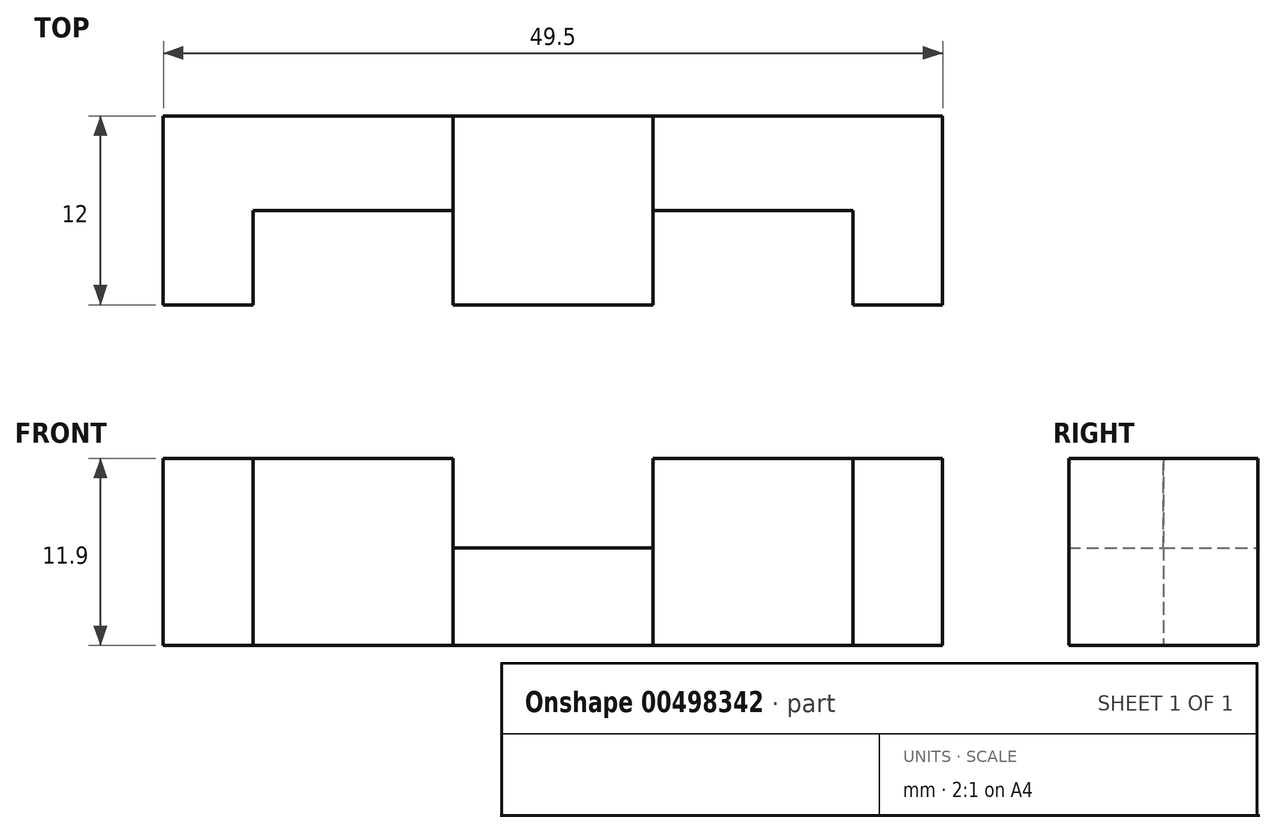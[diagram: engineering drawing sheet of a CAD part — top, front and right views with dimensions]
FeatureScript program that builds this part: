
annotation { "Feature Type Name" : "Feature", "Feature Type Description" : "" }
export const myFeature = defineFeature(function(context is Context, id is Id, definition is map)
    precondition{}
    {
        {
            var Q0;
            Q0=qCreatedBy(makeId("Front.planeOp"),FACE);
            var sketch = newSketch(context, id + "F0", { "sketchPlane" : qUnion([Q0])});
            skLineSegment(sketch, "E0.bottom", {"start": v(-12.84, 9.96) * mm, "end": v(36.66, 9.96) * mm});
            skLineSegment(sketch, "E0.top", {"start": v(-12.84, -1.94) * mm, "end": v(36.66, -1.94) * mm});
            skLineSegment(sketch, "E0.left", {"start": v(-12.84, 9.96) * mm, "end": v(-12.84, -1.94) * mm});
            skLineSegment(sketch, "E0.right", {"start": v(36.66, 9.96) * mm, "end": v(36.66, -1.94) * mm});
            skLineSegment(sketch, "E1", {"start": v(5.56, 9.96) * mm, "end": v(5.56, 4.28) * mm});
            skLineSegment(sketch, "E2", {"start": v(5.56, 4.28) * mm, "end": v(18.26, 4.28) * mm});
            skLineSegment(sketch, "E3", {"start": v(18.26, 4.28) * mm, "end": v(18.26, 9.96) * mm});
            skSolve(sketch);
        }
        {
            var Q0;
            Q0=makeQuery(id+"F0.imprint","IMPRINT",FACE,{"disambiguationData":[TD([[makeQuery(id+"F0.imprint","IMPRINT",EDGE,{"derivedFrom":sQuery(id+"F0.wireOp",EDGE,"E0.top")}),1.0]])]});
            extrude(context, id + "F1", {"entities" : qUnion([Q0]), "depth" : 6 * mm});
        }
        {
            var Q0;
            Q0=makeQuery(id+"F1.opExtrude","CAP_FACE",FACE,{"disambiguationData":[OSD([sQuery(id+"F0.wireOp",EDGE,"E0.bottom"),sQuery(id+"F0.wireOp",EDGE,"E0.top"),sQuery(id+"F0.wireOp",EDGE,"E0.left"),sQuery(id+"F0.wireOp",EDGE,"E0.right"),sQuery(id+"F0.wireOp",EDGE,"E1"),sQuery(id+"F0.wireOp",EDGE,"E2"),sQuery(id+"F0.wireOp",EDGE,"E3")])],"isStart":false});
            var sketch = newSketch(context, id + "F2", { "sketchPlane" : qUnion([Q0])});
            skLineSegment(sketch, "E4", {"start": v(30.96, 9.96) * mm, "end": v(30.96, -1.94) * mm});
            skLineSegment(sketch, "E5", {"start": v(-7.14, 9.96) * mm, "end": v(-7.14, -1.94) * mm});
            skLineSegment(sketch, "E6", {"start": v(5.56, 4.28) * mm, "end": v(5.56, -1.94) * mm});
            skLineSegment(sketch, "E7", {"start": v(18.26, 4.28) * mm, "end": v(18.26, -1.94) * mm});
            skSolve(sketch);
        }
        {
            var Q0;
            {var subQ0=sQuery(id+"F2.wireOp",EDGE,"E5");Q0=makeQuery(id+"F2.imprint","IMPRINT",FACE,{"disambiguationData":[TD([[makeQuery(id+"F2.imprint","IMPRINT",EDGE,{"derivedFrom":subQ0}),-1.0]])]});}
            var Q1;
            {var subQ0=sQuery(id+"F2.wireOp",EDGE,"E6");Q1=makeQuery(id+"F2.imprint","IMPRINT",FACE,{"disambiguationData":[TD([[makeQuery(id+"F2.imprint","IMPRINT",EDGE,{"derivedFrom":subQ0}),1.0]])]});}
            var Q2;
            {var subQ0=sQuery(id+"F2.wireOp",EDGE,"E4");Q2=makeQuery(id+"F2.imprint","IMPRINT",FACE,{"disambiguationData":[TD([[makeQuery(id+"F2.imprint","IMPRINT",EDGE,{"derivedFrom":subQ0}),1.0]])]});}
            extrude(context, id + "F3", {"entities" : qUnion([Q0, Q1, Q2]), "operationType" : NewBodyOperationType.ADD, "depth" : 6 * mm});
        }
    });
